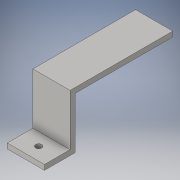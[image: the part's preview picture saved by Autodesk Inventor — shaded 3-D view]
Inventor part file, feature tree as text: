
AUTODESK INVENTOR PART (.ipt)
format: ipt  version: 2016 (Build 200138000, 138)  size: 105,472 bytes
history: native  units: in
note: dims shown in document units (in); Inventor stores cm internally (conversion verified against a paired STEP export)
features: extrude x2, sketch x2
ambient origin geometry x8: Origin, YZ Plane, XZ Plane, XY Plane, X Axis, Y Axis, Z Axis, Center Point
bodies: Solid1 (feature_tree)
feature tree (4):
  extrude  "Extrusion1"  Depth=0.5in
  extrude  "Extrusion2"  Depth=0.725in TaperAngle=0.0deg
  sketch  "Sketch1"  dims[d0=0.5in d1=0.5in]
  sketch  "Sketch2"  dims[d2=0.1in d6=0.725in d7=0.0in d8=0.1181in d9=0.725in d10=0.0in d11=1.0in d12=0.1in d13=2.0in]
